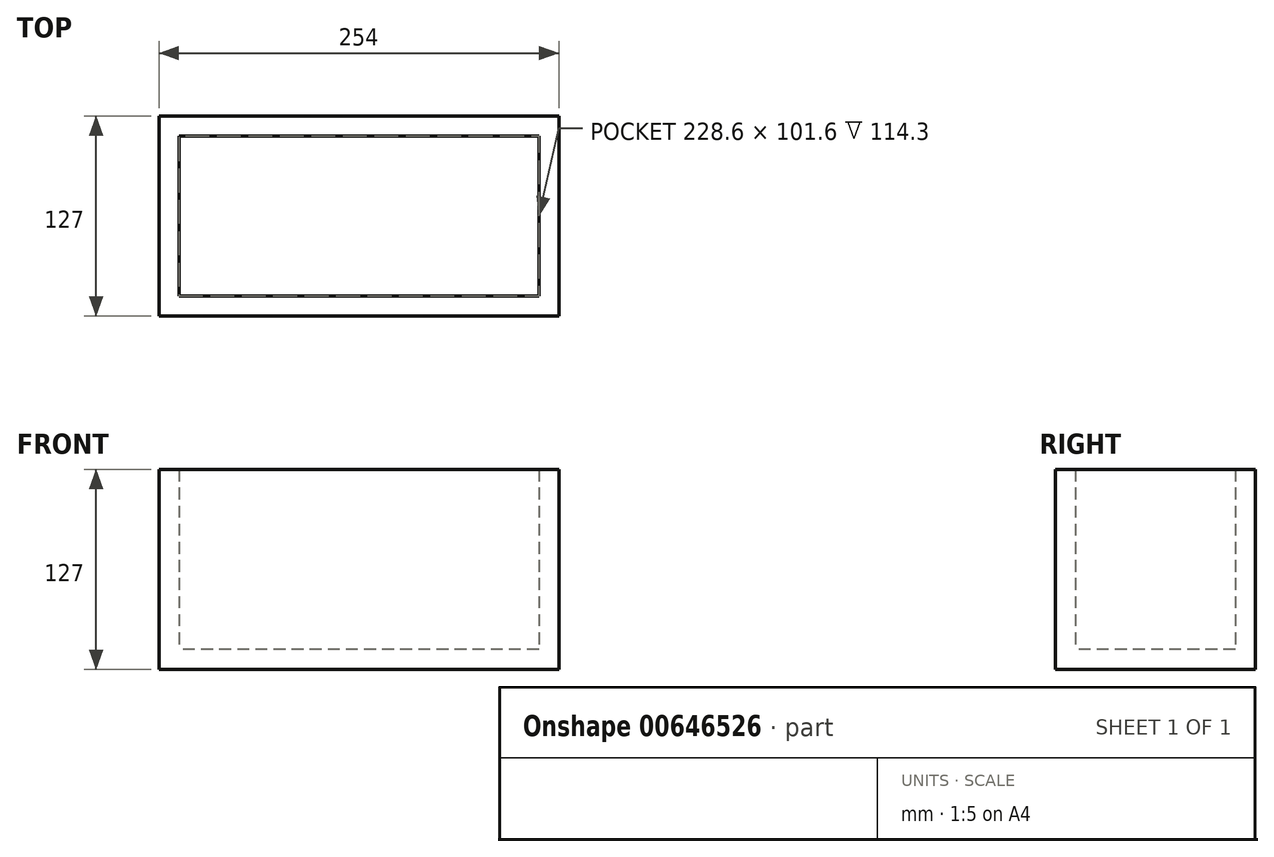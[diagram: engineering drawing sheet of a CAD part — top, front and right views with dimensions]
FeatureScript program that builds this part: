
annotation { "Feature Type Name" : "Feature", "Feature Type Description" : "" }
export const myFeature = defineFeature(function(context is Context, id is Id, definition is map)
    precondition{}
    {
        {
            var Q0;
            Q0=qCreatedBy(makeId("Top.planeOp"),FACE);
            var sketch = newSketch(context, id + "F0", { "sketchPlane" : qUnion([Q0])});
            skLineSegment(sketch, "E0.bottom", {"start": v(127, 63.5) * mm, "end": v(-127, 63.5) * mm});
            skLineSegment(sketch, "E0.top", {"start": v(127, -63.5) * mm, "end": v(-127, -63.5) * mm});
            skLineSegment(sketch, "E0.left", {"start": v(127, 63.5) * mm, "end": v(127, -63.5) * mm});
            skLineSegment(sketch, "E0.right", {"start": v(-127, 63.5) * mm, "end": v(-127, -63.5) * mm});
            skPoint(sketch, "E0.middle", {"position": v(0, 0) * mm});
            skSolve(sketch);
        }
        {
            var Q0;
            Q0=makeQuery(id+"F0.imprint","IMPRINT",FACE,{"disambiguationData":[TD([[makeQuery(id+"F0.imprint","IMPRINT",EDGE,{"derivedFrom":sQuery(id+"F0.wireOp",EDGE,"E0.bottom")}),1.0]])]});
            extrude(context, id + "F1", {"entities" : qUnion([Q0]), "endBound" : BoundingType.SYMMETRIC, "depth" : 127 * mm, "offsetDistance" : 25.4 * mm});
        }
        {
            var Q0;
            Q0=makeQuery(id+"F1.opExtrude","CAP_FACE",FACE,{"disambiguationData":[OSD([sQuery(id+"F0.wireOp",EDGE,"E0.bottom"),sQuery(id+"F0.wireOp",EDGE,"E0.top"),sQuery(id+"F0.wireOp",EDGE,"E0.left"),sQuery(id+"F0.wireOp",EDGE,"E0.right")])],"isStart":false});
            shell(context, id + "F2", {"entities" : qUnion([Q0]), "thickness" : 12.7 * mm});
        }
    });
